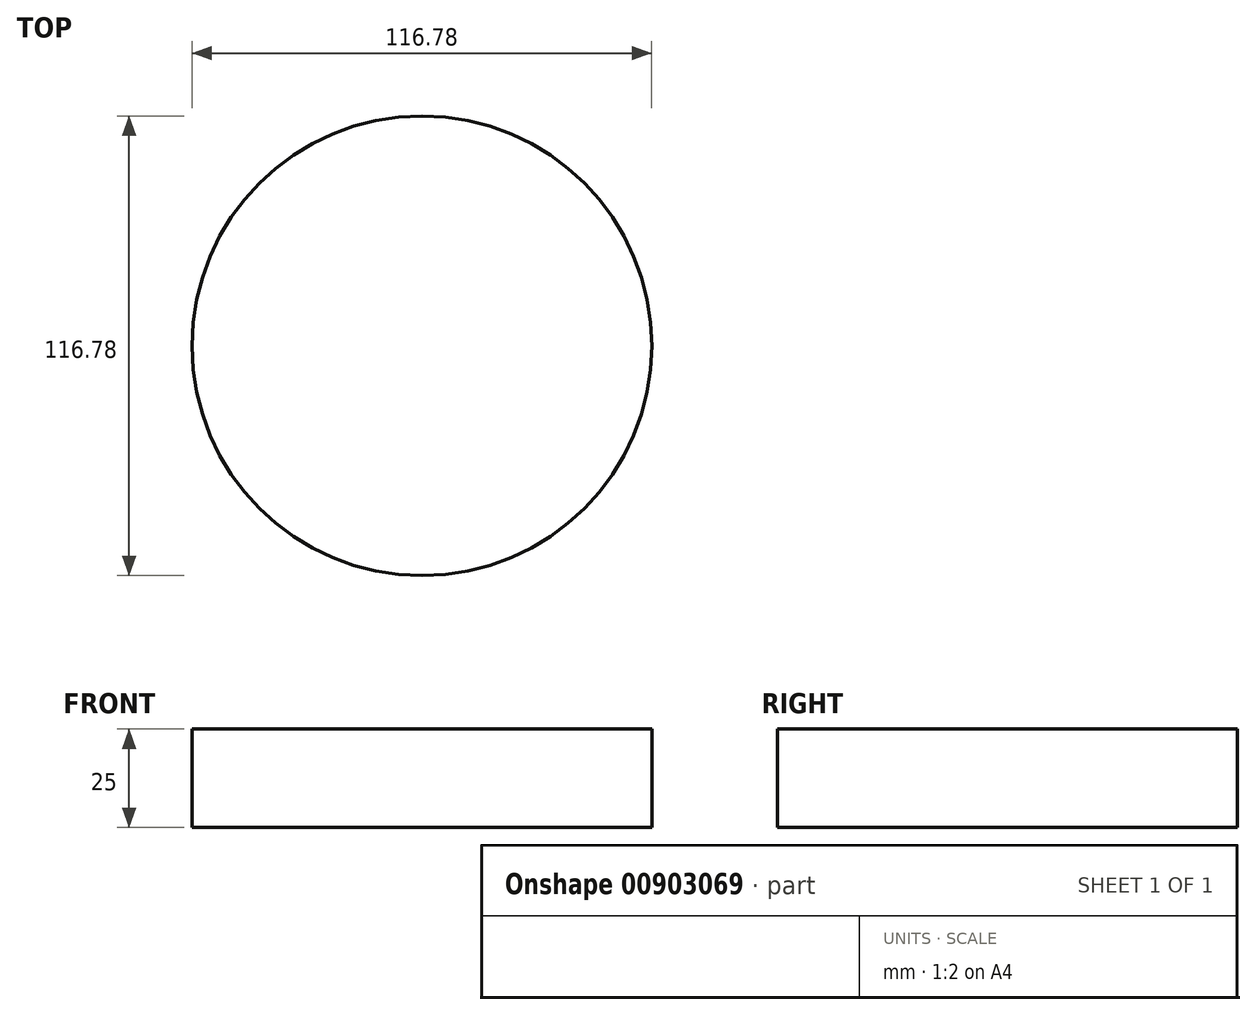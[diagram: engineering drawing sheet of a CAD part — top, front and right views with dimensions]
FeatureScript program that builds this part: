
annotation { "Feature Type Name" : "Feature", "Feature Type Description" : "" }
export const myFeature = defineFeature(function(context is Context, id is Id, definition is map)
    precondition{}
    {
        {
            var Q0;
            Q0=qCreatedBy(makeId("Top.planeOp"),FACE);
            var sketch = newSketch(context, id + "F0", { "sketchPlane" : qUnion([Q0])});
            skCircle(sketch, "E0", {"center": v(0, 0) * mm, "radius": 58.4 * mm});
            skSolve(sketch);
        }
        {
            var Q0;
            Q0=makeQuery(id+"F0.imprint","IMPRINT",FACE,{"disambiguationData":[TD([[makeQuery(id+"F0.imprint","IMPRINT",EDGE,{"derivedFrom":sQuery(id+"F0.wireOp",EDGE,"E0")}),1.0]])]});
            extrude(context, id + "F1", {"entities" : qUnion([Q0]), "depth" : 25 * mm, "offsetDistance" : 25 * mm});
        }
    });
